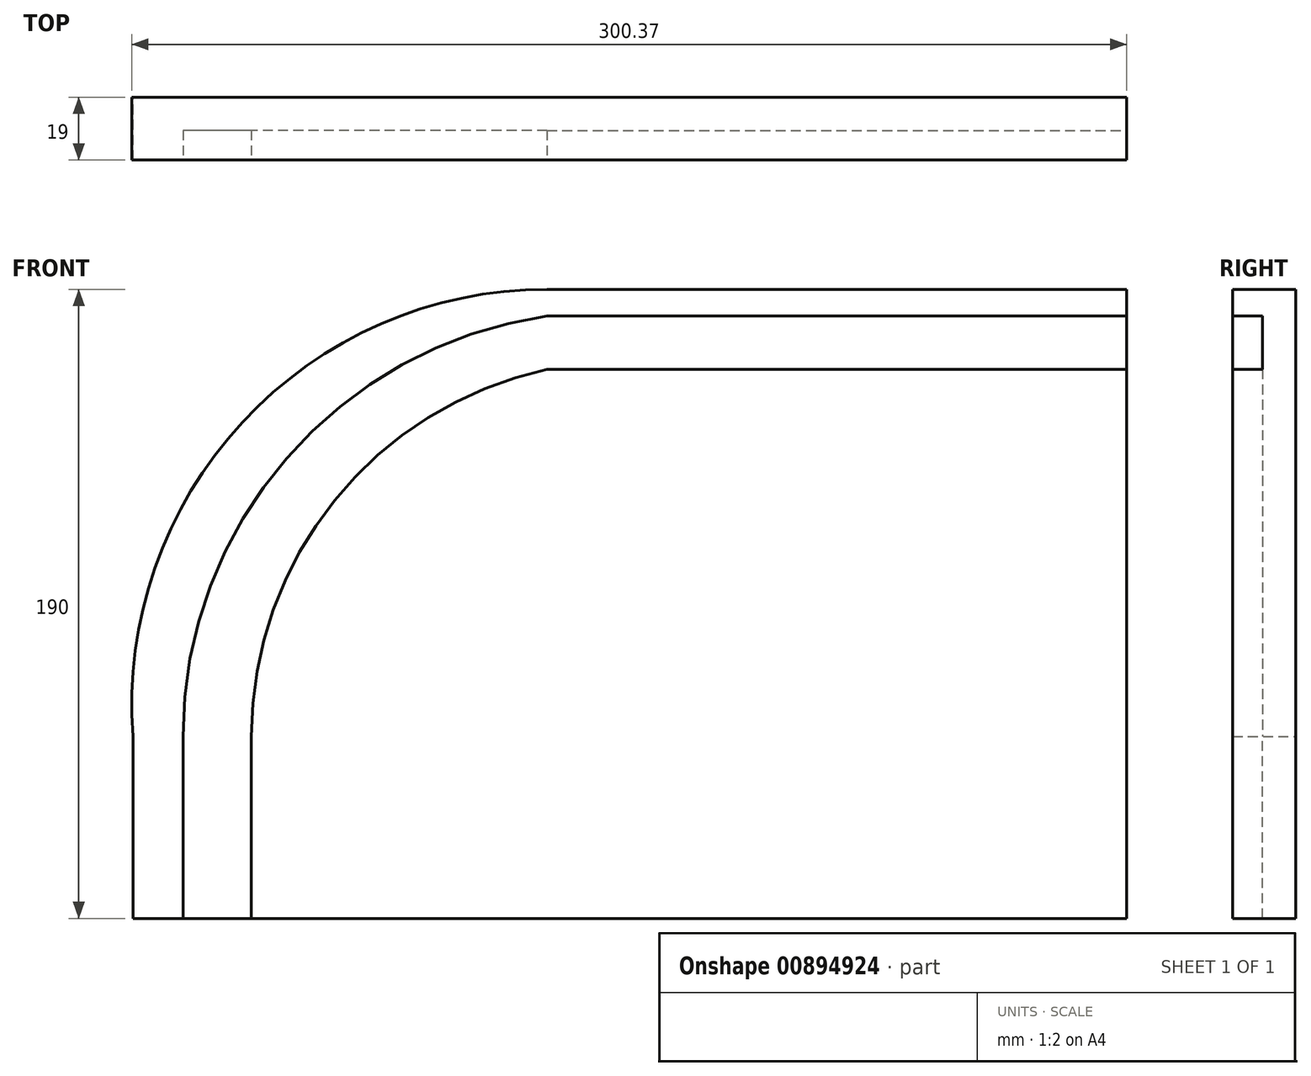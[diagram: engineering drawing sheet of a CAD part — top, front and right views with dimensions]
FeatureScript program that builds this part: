
annotation { "Feature Type Name" : "Feature", "Feature Type Description" : "" }
export const myFeature = defineFeature(function(context is Context, id is Id, definition is map)
    precondition{}
    {
        {
            var Q0;
            Q0=qCreatedBy(makeId("Front.planeOp"),FACE);
            var sketch = newSketch(context, id + "F0", { "sketchPlane" : qUnion([Q0])});
            skLineSegment(sketch, "E0", {"start": v(215.8, 91.66) * mm, "end": v(215.8, -98.34) * mm});
            skLineSegment(sketch, "E1", {"start": v(215.8, -98.34) * mm, "end": v(-84.2, -98.34) * mm});
            skLineSegment(sketch, "E2", {"start": v(-84.2, -98.34) * mm, "end": v(-84.2, -43.34) * mm});
            skLineSegment(sketch, "E3", {"start": v(215.8, 91.66) * mm, "end": v(40.8, 91.66) * mm});
            skArc(sketch, "E4", {"start": v(40.8, 91.66) * mm, "mid": v(-51.19, 51.47) * mm, "end": v(-84.2, -43.34) * mm});
            skSolve(sketch);
        }
        {
            var Q0;
            Q0 = qSketchRegion(id + "F0", true);
            extrude(context, id + "F1", {"entities" : qUnion([Q0]), "depth" : 19 * mm, "offsetDistance" : 25.4 * mm});
        }
        {
            var Q0;
            Q0=makeQuery(id+"F1.opExtrude","CAP_FACE",FACE,{"disambiguationData":[OSD([sQuery(id+"F0.wireOp",EDGE,"E0"),sQuery(id+"F0.wireOp",EDGE,"E1"),sQuery(id+"F0.wireOp",EDGE,"E2"),sQuery(id+"F0.wireOp",EDGE,"E3"),sQuery(id+"F0.wireOp",EDGE,"E4")])],"isStart":false});
            var sketch = newSketch(context, id + "F2", { "sketchPlane" : qUnion([Q0])});
            skPoint(sketch, "E5", {"position": v(-69.13, -98.34) * mm});
            skPoint(sketch, "E6", {"position": v(-48.48, -98.34) * mm});
            skPoint(sketch, "E7", {"position": v(-69.13, -43.34) * mm});
            skPoint(sketch, "E8", {"position": v(-48.48, -43.34) * mm});
            skPoint(sketch, "E9", {"position": v(215.8, 83.56) * mm});
            skPoint(sketch, "E10", {"position": v(215.8, 67.5) * mm});
            skPoint(sketch, "E11", {"position": v(40.8, 67.5) * mm});
            skPoint(sketch, "E12", {"position": v(40.8, 83.56) * mm});
            skLineSegment(sketch, "E13", {"start": v(-48.48, -43.34) * mm, "end": v(-48.48, -98.34) * mm});
            skLineSegment(sketch, "E14", {"start": v(-69.13, -98.34) * mm, "end": v(-69.13, -43.34) * mm});
            skLineSegment(sketch, "E15", {"start": v(40.8, 67.5) * mm, "end": v(215.8, 67.5) * mm});
            skLineSegment(sketch, "E16", {"start": v(40.8, 83.56) * mm, "end": v(215.8, 83.56) * mm});
            skArc(sketch, "E17", {"start": v(40.8, 83.56) * mm, "mid": v(-37.82, 40.6) * mm, "end": v(-69.13, -43.34) * mm});
            skArc(sketch, "E18", {"start": v(40.8, 67.5) * mm, "mid": v(-23.38, 27.82) * mm, "end": v(-48.48, -43.34) * mm});
            skSolve(sketch);
        }
        {
            var Q0;
            {var subQ1=sQuery(id+"F2.wireOp",EDGE,"E13");Q0=makeQuery(id+"F2.imprint","IMPRINT",FACE,{"disambiguationData":[TD([[makeQuery(id+"F2.imprint","IMPRINT",EDGE,{"derivedFrom":subQ1}),-1.0]])]});}
            extrude(context, id + "F3", {"entities" : qUnion([Q0]), "operationType" : NewBodyOperationType.REMOVE, "oppositeDirection" : true, "depth" : 9 * mm, "offsetDistance" : 25.4 * mm});
        }
    });
